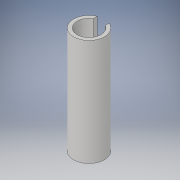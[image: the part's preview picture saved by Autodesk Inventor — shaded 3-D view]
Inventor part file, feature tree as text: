
AUTODESK INVENTOR PART (.ipt)
format: ipt  version: 2019 (Build 230136000, 136)  size: 319,488 bytes
history: native  units: mm
features: sketch x6, extrude x4, fillet x3, loft x2, other x2, plane x1
ambient origin geometry x8: Origin, YZ Plane, XZ Plane, XY Plane, X Axis, Y Axis, Z Axis, Center Point
bodies: Solid1 (feature_tree)
feature tree (18):
  extrude  "Extrusion1"  Depth=26.0mm
  extrude  "Extrusion2"  Depth=1.0mm
  extrude  "Extrusion3"  Depth=10.0mm
  sketch  "Sketch9"  dims[d7=20.0mm d8=10.0mm d9=0.0mm]
  plane  "Work Plane2"
  loft  "Loft1"
  extrude  "Extrusion6"  Depth=40.0mm
  loft  "Loft2"
  fillet  "Fillet1"  [1 undecoded]
  fillet  "Fillet2"  Radius=20.0mm
  fillet  "Fillet3"  Radius=20.0mm
  sketch  "Sketch1"  dims[d0=20.0mm d1=26.0mm]
  sketch  "Sketch2"  dims[d2=40.0mm d3=0.0mm d4=1.0mm]
  sketch  "Sketch3"  dims[d5=1.0mm d6=10.0mm]
  sketch  "Sketch10"  dims[d10=10.0mm d11=0.0mm d21=40.0mm]
  sketch  "Sketch11"  dims[d22=26.0mm d23=0.0mm d24=90.0deg d25=0.0mm d26=90.0deg d27=20.0mm d28=20.0mm d29=0.0mm d30=0.0mm d31=90.0deg d32=0.0mm d33=90.0deg d34=10.0mm d35=10.0mm d36=26.0mm d37=26.0mm d38=13.0mm d39=26.0mm d40=5.0mm]
  other  "Edges1"
  other  "Edges2"
note: 1 required parameter value undecoded (feature->parameter linkage not recoverable at this tier; creation-order binding heuristic only, values carry confidence <= 0.55)
